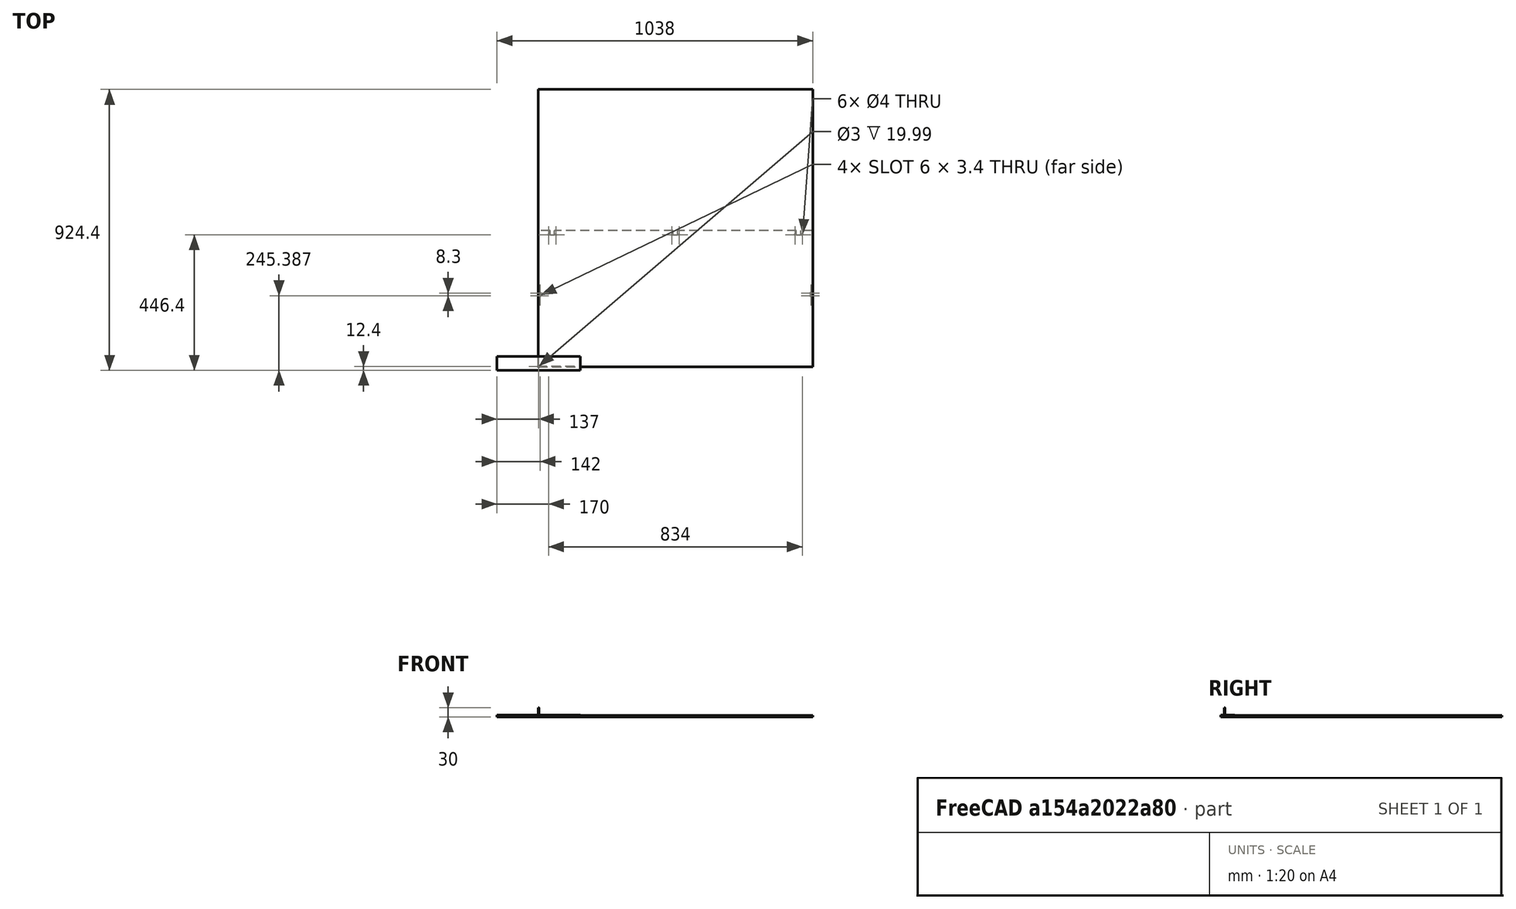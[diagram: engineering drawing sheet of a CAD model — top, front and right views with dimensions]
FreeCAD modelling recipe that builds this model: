
FCSTD DOCUMENT  (FreeCAD 0.22R37100 (Git))
Label: composit_stand12_PP_cut
License: All rights reserved
LicenseURL: http://en.wikipedia.org/wiki/All_rights_reserved
objects: Path::FeaturePython×11, App::DocumentObjectGroup×8, Part::FeaturePython×7, App::Link×2, App::FeaturePython×2
note: 12 computed .brp shape members not serialized (recipe doc carries the construction recipe); baked Part::Feature solids carry a one-line shape summary decoded from their .brp
EXTERNAL_REF file=composit_stand12.FCStd obj=Body005
EXTERNAL_REF file=composit_stand12.FCStd obj=Body016

FEATURE [App::Link] Link  label="dropper_fix_PP"
  LinkedObject = -> <external composit_stand12.FCStd>#Body005
FEATURE [App::FeaturePython] SetupSheet  # Path/CAM operation (typed FeaturePython)
  ClearanceHeightExpression = OpStockZMax+SetupSheet.ClearanceHeightOffset
  ClearanceHeightOffset = 5
  CoolantMode = 0
  CoolantModes = None | Flood | Mist
  FinalDepthExpression = OpFinalDepth
  HorizRapid = 0
  ProfileDirection = 1
  ProfileprocessCircles = true
  ProfileprocessHoles = true
  ProfileprocessPerimeter = true
  SafeHeightExpression = OpStockZMax+SetupSheet.SafeHeightOffset
  SafeHeightOffset = 3
  StartDepthExpression = OpStartDepth
  StepDownExpression = OpToolDiameter
  VertRapid = 0
FEATURE [Part::FeaturePython] Clone  label="Model-dropper_fix_PP"  # Draft clone (typed FeaturePython)
  AttacherType = Attacher::AttachEngine3D
  Fuse = false
  Objects = -> [Link]
  PathResource = Model
  Placement = pos=(136,11.4,5) rot=(0,1,0;3.14159rad)
  Scale = (1,1,1)
FEATURE [App::DocumentObjectGroup] Model
  Group = -> [Clone]
FEATURE [Part::FeaturePython] ToolBit  label="3.175mm Endmill"  # Path/CAM toolbit (typed FeaturePython)
  BitPropertyNames = Chipload | CuttingEdgeHeight | Diameter | Flutes | Length | Material | ShankDiameter | SpindleDirection
  BitShape = <path>
  Chipload = 0
  CuttingEdgeHeight = 30
  Diameter = 3.175
  Flutes = 0
  Length = 10
  Material = 0
  ShankDiameter = 3
  ShapeName = endmill
  SpindleDirection = 0
FEATURE [Path::FeaturePython] __175mm_Endmill  label="3.175mm Endmill001"  # Path/CAM operation (typed FeaturePython)
  HorizFeed = 51.6667
  HorizRapid = 0
  SpindleDir = 0
  SpindleSpeed = 18000
  Tool = -> ToolBit
  ToolNumber = 1
  VertFeed = 35
  VertRapid = 0
  expr: HorizRapid = SetupSheet.HorizRapid
  expr: VertRapid = SetupSheet.VertRapid
FEATURE [App::DocumentObjectGroup] Tools
  Group = -> [__175mm_Endmill]
FEATURE [Part::FeaturePython] Stock  # WARN: FeaturePython — macro-defined, semantics opaque (R4)
  Base = -> Model
  ExtXneg = 1
  ExtXpos = 1
  ExtYneg = 1
  ExtYpos = 1
  ExtZneg = 0
  ExtZpos = 1
  Placement = pos=(-136,-11.4,0) rot=(0,0,1;0rad)
  StockType = FromBase
FEATURE [Path::FeaturePython] Profile  # Path/CAM operation (typed FeaturePython)
  Active = false
  AreaParams:
    Tolerance = 1e-07
    FitArcs = True
    Simplify = False
    CleanDistance = 0.0
    Accuracy = 0.01
    Unit = 1.0
    MinArcPoints = 4
    MaxArcPoints = 100
    ClipperScale = 10000000.0
    Fill = 0
    Coplanar = 0
    Reorient = True
    Outline = False
    Explode = False
    OpenMode = 0
    Deflection = 0.01
    SubjectFill = 0
    ClipFill = 0
    Offset = -1.5875
    ExtraPass = 0
    Stepover = 0.0
    LastStepover = 0.0
    JoinType = 0
    EndType = 0
    MiterLimit = 2.0
    RoundPrecision = 0.0
    PocketMode = 0
    ToolRadius = 1.0
    PocketExtraOffset = 0.0
    PocketStepover = 0.0
    PocketLastStepover = 0.0
    FromCenter = False
    Angle = 45.0
    AngleShift = 0.0
    Shift = 0.0
    Thicken = False
    SectionCount = -1
    Stepdown = 1.0
    SectionOffset = 0.0
    SectionTolerance = 1e-06
    SectionMode = 2
    Project = False
  Base = -> [Clone]
  ClearanceHeight = 11
  CoolantMode = 0
  CycleTime = 00:00:12
  Direction = 1
  FinalDepth = 0
  HandleMultipleFeatures = 0
  JoinType = 0
  MiterLimit = 0.1
  OffsetExtra = 0
  OpFinalDepth = 0
  OpStartDepth = 6
  OpStockZMax = 6
  OpStockZMin = 0
  OpToolDiameter = 3.175
  PathParams = {'orientation': 1, 'feedrate': 51.666666666666664, 'feedrate_v': 35.0, 'verbose': True, 'resume_height': 9.000000000000007, 'retraction': 11.000000000000007, 'return_end': True, 'preamble': False, 'start': Vector (249.59218891539706, 31.331318499196566, 11.000000000000007)}
  SafeHeight = 9
  Side = 0
  SplitArcs = false
  StartDepth = 6
  StartPoint = (0,0,0)
  StepDown = 10
  ToolController = -> __175mm_Endmill
  UseComp = true
  UseStartPoint = false
  processCircles = true
  processHoles = true
  processPerimeter = false
  expr: ClearanceHeight = OpStockZMax + SetupSheet.ClearanceHeightOffset
  expr: FinalDepth = OpFinalDepth
  expr: SafeHeight = OpStockZMax + SetupSheet.SafeHeightOffset
  expr: StartDepth = OpStartDepth
FEATURE [Path::FeaturePython] Profile001  # Path/CAM operation (typed FeaturePython)
  Active = true
  AreaParams:
    Tolerance = 1e-07
    FitArcs = True
    Simplify = False
    CleanDistance = 0.0
    Accuracy = 0.01
    Unit = 1.0
    MinArcPoints = 4
    MaxArcPoints = 100
    ClipperScale = 10000000.0
    Fill = 0
    Coplanar = 0
    Reorient = True
    Outline = False
    Explode = False
    OpenMode = 0
    Deflection = 0.01
    SubjectFill = 0
    ClipFill = 0
    Offset = 1.5875
    ExtraPass = 0
    Stepover = 0.0
    LastStepover = 0.0
    JoinType = 0
    EndType = 0
    MiterLimit = 2.0
    RoundPrecision = 0.0
    PocketMode = 0
    ToolRadius = 1.0
    PocketExtraOffset = 0.0
    PocketStepover = 0.0
    PocketLastStepover = 0.0
    FromCenter = False
    Angle = 45.0
    AngleShift = 0.0
    Shift = 0.0
    Thicken = False
    SectionCount = -1
    Stepdown = 1.0
    SectionOffset = 0.0
    SectionTolerance = 1e-06
    SectionMode = 2
    Project = False
  ClearanceHeight = 11
  CoolantMode = 0
  CycleTime = 00:00:18
  Direction = 1
  FinalDepth = 0
  HandleMultipleFeatures = 0
  JoinType = 0
  MiterLimit = 0.1
  OffsetExtra = 0
  OpFinalDepth = 0
  OpStartDepth = 6
  OpStockZMax = 6
  OpStockZMin = 0
  OpToolDiameter = 3.175
  PathParams:
    orientation = 0
    feedrate = 51.666666666666664
    feedrate_v = 35.0
    verbose = True
    resume_height = 9.000000000000007
    retraction = 11.000000000000007
    return_end = True
    preamble = False
  SafeHeight = 9
  Side = 0
  SplitArcs = false
  StartDepth = 6
  StartPoint = (0,0,0)
  StepDown = 10
  ToolController = -> __175mm_Endmill
  UseComp = true
  UseStartPoint = false
  processCircles = false
  processHoles = false
  processPerimeter = true
  expr: ClearanceHeight = OpStockZMax + SetupSheet.ClearanceHeightOffset
  expr: FinalDepth = OpFinalDepth
  expr: SafeHeight = OpStockZMax + SetupSheet.SafeHeightOffset
  expr: StartDepth = OpStartDepth
FEATURE [Path::FeaturePython] Pocket_Shape  # Path/CAM operation (typed FeaturePython)
  Active = true
  AreaParams:
    Tolerance = 1e-07
    FitArcs = True
    Simplify = False
    CleanDistance = 0.0
    Accuracy = 0.01
    Unit = 1.0
    MinArcPoints = 4
    MaxArcPoints = 100
    ClipperScale = 10000000.0
    Fill = 0
    Coplanar = 0
    Reorient = True
    Outline = False
    Explode = False
    OpenMode = 0
    Deflection = 0.01
    SubjectFill = 0
    ClipFill = 0
    Offset = 0.0
    ExtraPass = 0
    Stepover = 0.0
    LastStepover = 0.0
    JoinType = 0
    EndType = 0
    MiterLimit = 2.0
    RoundPrecision = 0.0
    PocketMode = 2
    ToolRadius = 1.5875
    PocketExtraOffset = 0.0
    PocketStepover = 1.5875
    PocketLastStepover = 0.0
    FromCenter = True
    Angle = 45.0
    AngleShift = 0.0
    Shift = 0.0
    Thicken = False
    SectionCount = -1
    Stepdown = 1.0
    SectionOffset = 0.0
    SectionTolerance = 1e-06
    SectionMode = 2
    Project = False
  Base = -> [Clone]
  ClearanceHeight = 11
  CoolantMode = 0
  CutMode = 0
  CycleTime = 00:00:30
  ExtensionCorners = true
  ExtensionLengthDefault = 1.5875
  ExtraOffset = 0
  FinalDepth = 2.5
  FinishDepth = 0
  KeepToolDown = true
  MinTravel = true
  OffsetPattern = 1
  OpFinalDepth = 2.5
  OpStartDepth = 6
  OpStockZMax = 6
  OpStockZMin = 0
  OpToolDiameter = 3.175
  PathParams = {'orientation': 1, 'feedrate': 51.666666666666664, 'feedrate_v': 35.0, 'verbose': True, 'resume_height': 9.000000000000007, 'retraction': 11.000000000000007, 'return_end': True, 'preamble': False, 'threshold': 3.1765874999999997, 'start': Vector (171.24943169999997, 31.399999999999974, 2.5000000000000004)}
  PocketLastStepOver = 0
  SafeHeight = 9
  SplitArcs = false
  StartAt = 0
  StartDepth = 6
  StartPoint = (0,0,0)
  StepDown = 10
  StepOver = 50
  ToolController = -> __175mm_Endmill
  UseOutline = true
  UseRestMachining = false
  UseStartPoint = false
  ZigZagAngle = 45
  expr: ClearanceHeight = OpStockZMax + SetupSheet.ClearanceHeightOffset
  expr: ExtensionLengthDefault = OpToolDiameter / 2
  expr: FinalDepth = OpFinalDepth
  expr: SafeHeight = OpStockZMax + SetupSheet.SafeHeightOffset
  expr: StartDepth = OpStartDepth
FEATURE [Path::FeaturePython] Deburr  # Path/CAM operation (typed FeaturePython)
  Active = true
  Base = -> [Clone]
  ClearanceHeight = 11
  CoolantMode = 0
  CycleTime = 00:00:13
  Direction = 0
  EntryPoint = 0
  ExtraDepth = 0
  Join = 0
  OpStockZMax = 6
  OpStockZMin = 0
  OpToolDiameter = 3.175
  SafeHeight = 9
  Side = 0
  StartDepth = 6
  StepDown = 0
  ToolController = -> __175mm_Endmill
  Width = 1.6
  expr: ClearanceHeight = OpStockZMax + SetupSheet.ClearanceHeightOffset
  expr: SafeHeight = OpStockZMax + SetupSheet.SafeHeightOffset
  expr: StepDown = 0 mm
FEATURE [Path::FeaturePython] Array  # Path/CAM operation (typed FeaturePython)
  Active = true
  Angle = 0
  Base = -> [Profile,Pocket_Shape,Deburr,Profile001]
  Centre = (0,0,0)
  Copies = 2
  CopiesX = 0
  CopiesY = 0
  JitterMagnitude = (0,0,0)
  JitterPercent = 0
  JitterSeed = 0
  Offset = (0,46.6,0)
  SwapDirection = false
  ToolController = -> __175mm_Endmill
  Type = 0
FEATURE [App::DocumentObjectGroup] Operations
  Group = -> [Profile,Pocket_Shape,Deburr,Profile001,Array]
FEATURE [Path::FeaturePython] Job  # Path/CAM operation (typed FeaturePython)
  CycleTime = 00:01:01
  Fixtures = G54
  GeometryTolerance = 0.01
  JobType = 0
  LastPostProcessDate = 2024-06-07 14:32:44.748301
  LastPostProcessOutput = <path>
  Model = -> Model
  Operations = -> Operations
  OrderOutputBy = 2
  PostProcessor = 13
  PostProcessorOutputFile = <path>/%j.tap
  SetupSheet = -> SetupSheet
  SplitOutput = false
  Stock = -> Stock
  Tools = -> Tools
FEATURE [App::Link] Link001  label="door_plexiglass"
  LinkPlacement = pos=(0,0,0) rot=(-1,0,0;1.5708rad)
  LinkedObject = -> <external composit_stand12.FCStd>#Body016
  Placement = pos=(0,0,0) rot=(-1,0,0;1.5708rad)
FEATURE [App::DocumentObjectGroup] Group  label="parts"
  Group = -> [Link,Link001]
FEATURE [App::FeaturePython] SetupSheet001  # Path/CAM operation (typed FeaturePython)
  ClearanceHeightExpression = OpStockZMax+SetupSheet001.ClearanceHeightOffset
  ClearanceHeightOffset = 5
  CoolantMode = 0
  CoolantModes = None | Flood | Mist
  FinalDepthExpression = OpFinalDepth
  HorizRapid = 0
  ProfileDirection = 1
  ProfileprocessCircles = true
  ProfileprocessHoles = true
  ProfileprocessPerimeter = true
  SafeHeightExpression = OpStockZMax+SetupSheet001.SafeHeightOffset
  SafeHeightOffset = 3
  StartDepthExpression = OpStartDepth
  StepDownExpression = OpToolDiameter
  VertRapid = 0
FEATURE [Part::FeaturePython] Clone001  label="Model-door_plexiglass"  # Draft clone (typed FeaturePython)
  AttacherType = Attacher::AttachEngine3D
  Fuse = false
  Objects = -> [Link001]
  PathResource = Model
  Placement = pos=(900,0,0) rot=(0.57735,0.57735,-0.57735;4.18879rad)
  Scale = (1,1,1)
FEATURE [Part::FeaturePython] ToolBit001  label="3.175mm Endmill003"  # Path/CAM toolbit (typed FeaturePython)
  BitPropertyNames = Chipload | CuttingEdgeHeight | Diameter | Flutes | Length | Material | ShankDiameter | SpindleDirection
  BitShape = <path>
  Chipload = 0
  CuttingEdgeHeight = 30
  Diameter = 3.175
  Flutes = 0
  Length = 10
  Material = 0
  ShankDiameter = 3
  ShapeName = endmill
  SpindleDirection = 0
FEATURE [Path::FeaturePython] __175mm_Endmill001  label="3.175mm Endmill002"  # Path/CAM operation (typed FeaturePython)
  HorizFeed = 51.6667
  HorizRapid = 0
  SpindleDir = 0
  SpindleSpeed = 18000
  Tool = -> ToolBit001
  ToolNumber = 1
  VertFeed = 35
  VertRapid = 0
  expr: HorizRapid = SetupSheet001.HorizRapid
  expr: VertRapid = SetupSheet001.VertRapid
FEATURE [App::DocumentObjectGroup] Tools001
  Group = -> [__175mm_Endmill001]
FEATURE [Part::FeaturePython] Clone002  label="Model-door_plexiglass001"  # Draft clone (typed FeaturePython)
  AttacherType = Attacher::AttachEngine3D
  Fuse = false
  Objects = -> [Link001]
  PathResource = Model
  Placement = pos=(0,9e-16,0) rot=(-1,0,0;1.5708rad)
  Scale = (1,1,1)
FEATURE [App::DocumentObjectGroup] Model001
  Group = -> [Clone001,Clone002]
FEATURE [Part::FeaturePython] Stock001  # WARN: FeaturePython — macro-defined, semantics opaque (R4)
  Base = -> Model001
  ExtXneg = 1
  ExtXpos = 1
  ExtYneg = 1
  ExtYpos = 1
  ExtZneg = 0
  ExtZpos = 1
  Placement = pos=(0,-9e-16,0) rot=(0,0,1;0rad)
  StockType = FromBase
FEATURE [Path::FeaturePython] Profile002  # Path/CAM operation (typed FeaturePython)
  Active = true
  AreaParams:
    Tolerance = 1e-07
    FitArcs = True
    Simplify = False
    CleanDistance = 0.0
    Accuracy = 0.01
    Unit = 1.0
    MinArcPoints = 4
    MaxArcPoints = 100
    ClipperScale = 10000000.0
    Fill = 0
    Coplanar = 0
    Reorient = True
    Outline = False
    Explode = False
    OpenMode = 0
    Deflection = 0.01
    SubjectFill = 0
    ClipFill = 0
    Offset = -1.5875
    ExtraPass = 0
    Stepover = 0.0
    LastStepover = 0.0
    JoinType = 0
    EndType = 0
    MiterLimit = 2.0
    RoundPrecision = 0.0
    PocketMode = 0
    ToolRadius = 1.0
    PocketExtraOffset = 0.0
    PocketStepover = 0.0
    PocketLastStepover = 0.0
    FromCenter = False
    Angle = 45.0
    AngleShift = 0.0
    Shift = 0.0
    Thicken = False
    SectionCount = -1
    Stepdown = 1.0
    SectionOffset = 0.0
    SectionTolerance = 1e-06
    SectionMode = 2
    Project = False
  Base = -> [Clone002]
  ClearanceHeight = 10
  CoolantMode = 0
  CycleTime = 00:00:41
  Direction = 1
  FinalDepth = 0
  HandleMultipleFeatures = 0
  JoinType = 0
  MiterLimit = 0.1
  OffsetExtra = 0
  OpFinalDepth = 0
  OpStartDepth = 5
  OpStockZMax = 5
  OpStockZMin = 0
  OpToolDiameter = 3.175
  PathParams = {'orientation': 1, 'feedrate': 51.666666666666664, 'feedrate_v': 35.0, 'verbose': True, 'resume_height': 8.000000000000203, 'retraction': 10.000000000000203, 'return_end': True, 'preamble': False, 'start': Vector (210.1037548157733, 899.0003973583006, 10.000000000000203)}
  SafeHeight = 8
  Side = 0
  SplitArcs = false
  StartDepth = 5
  StartPoint = (0,0,0)
  StepDown = 3.175
  ToolController = -> __175mm_Endmill001
  UseComp = true
  UseStartPoint = false
  processCircles = true
  processHoles = true
  processPerimeter = false
  expr: ClearanceHeight = OpStockZMax + SetupSheet001.ClearanceHeightOffset
  expr: FinalDepth = OpFinalDepth
  expr: SafeHeight = OpStockZMax + SetupSheet001.SafeHeightOffset
  expr: StartDepth = OpStartDepth
  expr: StepDown = OpToolDiameter
FEATURE [Path::FeaturePython] Profile003  # Path/CAM operation (typed FeaturePython)
  Active = true
  AreaParams:
    Tolerance = 1e-07
    FitArcs = True
    Simplify = False
    CleanDistance = 0.0
    Accuracy = 0.01
    Unit = 1.0
    MinArcPoints = 4
    MaxArcPoints = 100
    ClipperScale = 10000000.0
    Fill = 0
    Coplanar = 0
    Reorient = True
    Outline = False
    Explode = False
    OpenMode = 0
    Deflection = 0.01
    SubjectFill = 0
    ClipFill = 0
    Offset = 1.5875
    ExtraPass = 0
    Stepover = 0.0
    LastStepover = 0.0
    JoinType = 0
    EndType = 0
    MiterLimit = 2.0
    RoundPrecision = 0.0
    PocketMode = 0
    ToolRadius = 1.0
    PocketExtraOffset = 0.0
    PocketStepover = 0.0
    PocketLastStepover = 0.0
    FromCenter = False
    Angle = 45.0
    AngleShift = 0.0
    Shift = 0.0
    Thicken = False
    SectionCount = -1
    Stepdown = 1.0
    SectionOffset = 0.0
    SectionTolerance = 1e-06
    SectionMode = 2
    Project = False
  Base = -> [Clone002]
  ClearanceHeight = 10
  CoolantMode = 0
  CycleTime = 00:02:08
  Direction = 1
  FinalDepth = 0
  HandleMultipleFeatures = 0
  JoinType = 0
  MiterLimit = 0.1
  OffsetExtra = 0
  OpFinalDepth = 0
  OpStartDepth = 5
  OpStockZMax = 5
  OpStockZMin = 0
  OpToolDiameter = 3.175
  PathParams:
    orientation = 0
    feedrate = 51.666666666666664
    feedrate_v = 35.0
    verbose = True
    resume_height = 8.000000000000203
    retraction = 10.000000000000203
    return_end = True
    preamble = False
  SafeHeight = 8
  Side = 0
  SplitArcs = false
  StartDepth = 5
  StartPoint = (0,0,0)
  StepDown = 3.175
  ToolController = -> __175mm_Endmill001
  UseComp = true
  UseStartPoint = false
  processCircles = false
  processHoles = false
  processPerimeter = true
  expr: Base = <<Profile002>>.Base
  expr: ClearanceHeight = OpStockZMax + SetupSheet001.ClearanceHeightOffset
  expr: FinalDepth = OpFinalDepth
  expr: SafeHeight = OpStockZMax + SetupSheet001.SafeHeightOffset
  expr: StartDepth = OpStartDepth
  expr: StepDown = OpToolDiameter
FEATURE [App::DocumentObjectGroup] Operations001
  Group = -> [Profile002,Profile003]
FEATURE [Path::FeaturePython] Job001  label="dver"  # Path/CAM operation (typed FeaturePython)
  CycleTime = 00:02:49
  Fixtures = G54
  GeometryTolerance = 0.01
  JobType = 0
  LastPostProcessDate = 2024-08-07 16:01:42.148983
  LastPostProcessOutput = <path> \n/mnt/flash/dver-1.tap
  Model = -> Model001
  Operations = -> Operations001
  OrderOutputBy = 2
  PostProcessor = 13
  PostProcessorOutputFile = <path>/%j.tap
  SetupSheet = -> SetupSheet001
  SplitOutput = true
  Stock = -> Stock001
  Tools = -> Tools001
FEATURE [App::DocumentObjectGroup] Group001  label="jobs"
  Group = -> [Job,Job001]
note: 6 file-system paths scrubbed to <path> (originals preserved in the JSON sidecar)

RESOLVED EXTERNAL PARTS (link-assembly join: the EXTERNAL_REF files above that resolve inside this repo's crawl, each included once):
---- part composit_stand12.FCStd = doc fcstd_02e919d733df (291737 chars; too large to inline — full recipe in that document) ----
